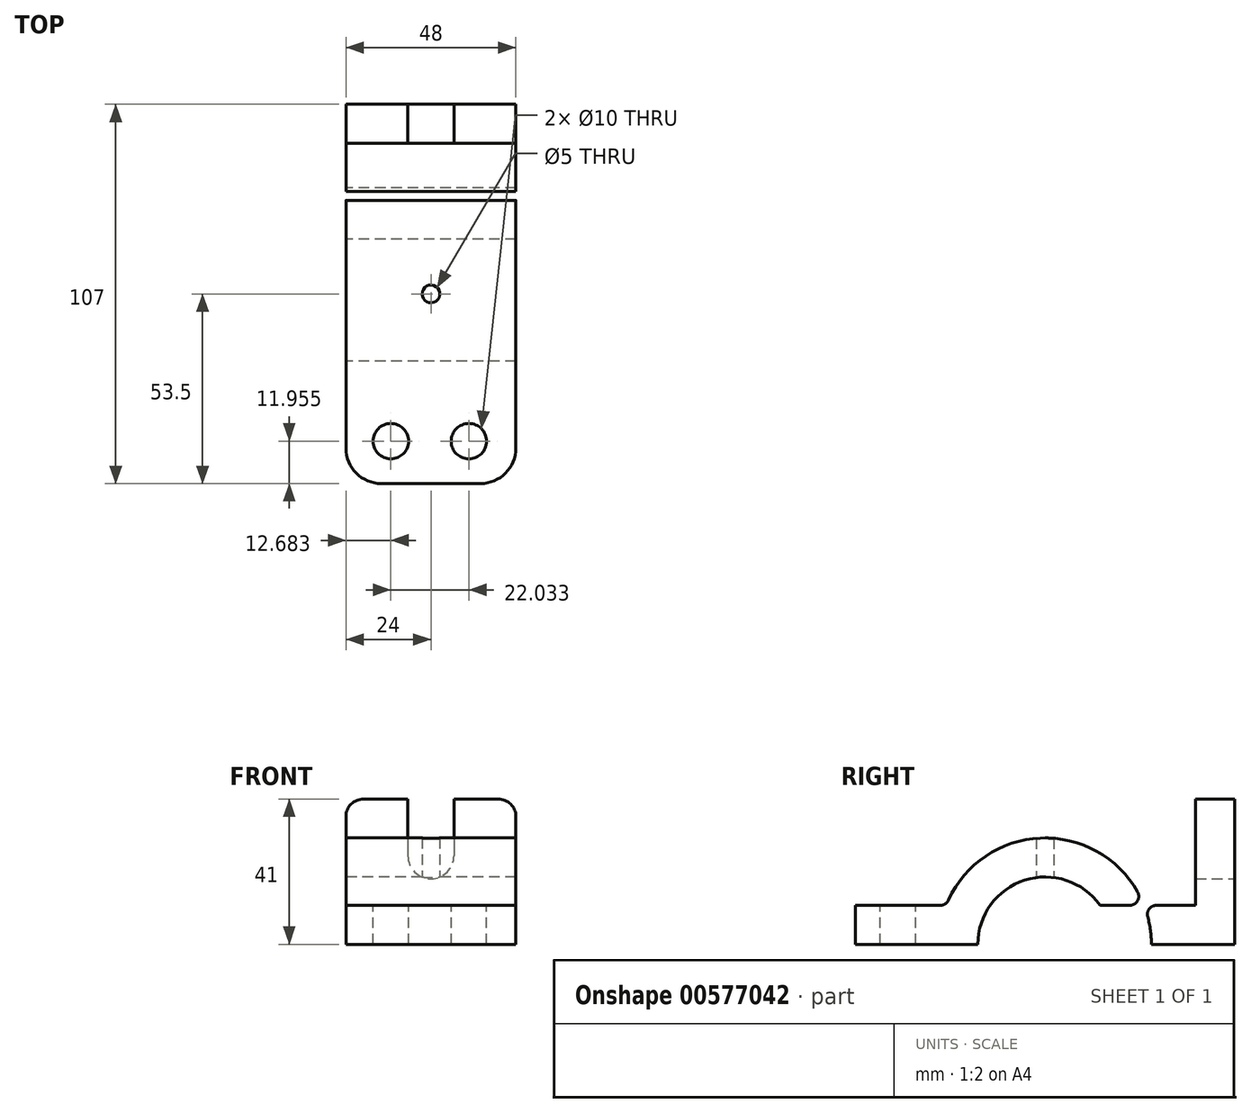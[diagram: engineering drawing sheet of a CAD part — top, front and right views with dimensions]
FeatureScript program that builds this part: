
annotation { "Feature Type Name" : "Feature", "Feature Type Description" : "" }
export const myFeature = defineFeature(function(context is Context, id is Id, definition is map)
    precondition{}
    {
        {
            var Q0;
            Q0=qCreatedBy(makeId("Right.planeOp"),FACE);
            var sketch = newSketch(context, id + "F0", { "sketchPlane" : qUnion([Q0])});
            skLineSegment(sketch, "E0", {"start": v(53.5, 0) * mm, "end": v(-53.5, 0) * mm});
            skLineSegment(sketch, "E1", {"start": v(0, 0) * mm, "end": v(53.5, 0) * mm});
            skArc(sketch, "E2", {"start": v(30, 0) * mm, "mid": v(0, 30) * mm, "end": v(-30, 0) * mm});
            skArc(sketch, "E3", {"start": v(19, 0) * mm, "mid": v(0, 19) * mm, "end": v(-19, 0) * mm});
            skLineSegment(sketch, "E4", {"start": v(53.5, 0) * mm, "end": v(53.5, 41) * mm});
            skLineSegment(sketch, "E5", {"start": v(53.5, 41) * mm, "end": v(42.5, 41) * mm});
            skLineSegment(sketch, "E6", {"start": v(42.5, 41) * mm, "end": v(42.5, 0) * mm});
            skLineSegment(sketch, "E7", {"start": v(-53.5, 0) * mm, "end": v(-53.5, 11) * mm});
            skLineSegment(sketch, "E8", {"start": v(-53.5, 11) * mm, "end": v(42.5, 11) * mm});
            skSolve(sketch);
        }
        {
            var Q0;
            {var subQ0=sQuery(id+"F0.wireOp",EDGE,"E7");Q0=makeQuery(id+"F0.imprint","IMPRINT",FACE,{"disambiguationData":[TD([[makeQuery(id+"F0.imprint","IMPRINT",EDGE,{"derivedFrom":subQ0}),-1.0]])]});}
            var Q1;
            {var subQ0=sQuery(id+"F0.wireOp",EDGE,"E2");var subQ1=sQuery(id+"F0.wireOp",EDGE,"E0");var subQ2=makeQuery(id+"F0.imprint","INTERSECT",VERTEX,{"derivedFrom":[subQ1,subQ0]});Q1=makeQuery(id+"F0.imprint","IMPRINT",FACE,{"disambiguationData":[TD([[makeQuery(id+"F0.imprint","IMPRINT",EDGE,{"disambiguationData":[TD([[subQ2,1.0]])],"derivedFrom":subQ1}),-1.0]])]});}
            var Q2;
            {var subQ0=sQuery(id+"F0.wireOp",EDGE,"E8");var subQ1=sQuery(id+"F0.wireOp",EDGE,"E2");var subQ2=makeQuery(id+"F0.imprint","INTERSECT",VERTEX,{"disambiguationData":[OD(0.0)],"derivedFrom":[subQ1,subQ0]});Q2=makeQuery(id+"F0.imprint","IMPRINT",FACE,{"disambiguationData":[TD([[makeQuery(id+"F0.imprint","IMPRINT",EDGE,{"disambiguationData":[TD([[subQ2,-1.0]])],"derivedFrom":subQ1}),1.0]])]});}
            var Q3;
            {var subQ0=sQuery(id+"F0.wireOp",EDGE,"E2");var subQ1=sQuery(id+"F0.wireOp",EDGE,"E1");var subQ2=makeQuery(id+"F0.imprint","INTERSECT",VERTEX,{"derivedFrom":[subQ1,subQ0]});Q3=makeQuery(id+"F0.imprint","IMPRINT",FACE,{"disambiguationData":[TD([[makeQuery(id+"F0.imprint","IMPRINT",EDGE,{"disambiguationData":[TD([[subQ2,1.0]])],"derivedFrom":subQ1}),1.0]])]});}
            var Q4;
            {var subQ0=sQuery(id+"F0.wireOp",EDGE,"E2");var subQ1=sQuery(id+"F0.wireOp",EDGE,"E1");var subQ2=makeQuery(id+"F0.imprint","INTERSECT",VERTEX,{"derivedFrom":[subQ1,subQ0]});Q4=makeQuery(id+"F0.imprint","IMPRINT",FACE,{"disambiguationData":[TD([[makeQuery(id+"F0.imprint","IMPRINT",EDGE,{"disambiguationData":[TD([[subQ2,-1.0]])],"derivedFrom":subQ1}),1.0]])]});}
            var Q5;
            {var subQ3=sQuery(id+"F0.wireOp",EDGE,"E4");Q5=makeQuery(id+"F0.imprint","IMPRINT",FACE,{"disambiguationData":[TD([[makeQuery(id+"F0.imprint","IMPRINT",EDGE,{"derivedFrom":subQ3}),1.0]])]});}
            extrude(context, id + "F1", {"entities" : qUnion([Q0, Q1, Q2, Q3, Q4, Q5]), "endBound" : BoundingType.SYMMETRIC, "depth" : 48 * mm, "offsetDistance" : 25.4 * mm});
        }
        {
            var Q0;
            Q0=makeQuery(id+"F1.opExtrude","CAP_EDGE",EDGE,{"disambiguationData":[OSD([sQuery(id+"F0.wireOp",EDGE,"E5")])],"isStart":false});
            fillet(context, id + "F2", {"entities" : qUnion([Q0]), "radius" : 5 * mm, "tangentPropagation" : true, "allowEdgeOverflow" : false});
        }
        {
            var Q0;
            Q0=makeQuery(id+"F1.opExtrude","CAP_EDGE",EDGE,{"disambiguationData":[OSD([sQuery(id+"F0.wireOp",EDGE,"E5")])],"isStart":true});
            fillet(context, id + "F3", {"entities" : qUnion([Q0]), "radius" : 5 * mm, "tangentPropagation" : true, "allowEdgeOverflow" : false});
        }
        {
            var Q0;
            Q0=makeQuery(id+"F1.opExtrude","SWEPT_FACE",FACE,{"disambiguationData":[OSD([sQuery(id+"F0.wireOp",EDGE,"E4")])]});
            var sketch = newSketch(context, id + "F4", { "sketchPlane" : qUnion([Q0])});
            skPoint(sketch, "E9", {"position": v(0, 41) * mm});
            skLineSegment(sketch, "E10", {"start": v(-6.5, 41) * mm, "end": v(6.5, 41) * mm});
            skLineSegment(sketch, "E11", {"start": v(0, 0) * mm, "end": v(0, 25) * mm});
            skLineSegment(sketch, "E12", {"start": v(-6.5, 41) * mm, "end": v(-6.5, 25) * mm});
            skLineSegment(sketch, "E13", {"start": v(6.5, 41) * mm, "end": v(6.5, 25) * mm});
            skCircle(sketch, "E14", {"center": v(0, 25) * mm, "radius": 6.5 * mm});
            skSolve(sketch);
        }
        {
            var Q0;
            {var subQ0=sQuery(id+"F4.wireOp",EDGE,"E14");var subQ1=makeQuery(id+"F4.imprint","INTERSECT",VERTEX,{"derivedFrom":[sQuery(id+"F4.wireOp",EDGE,"E12"),subQ0]});Q0=makeQuery(id+"F4.imprint","IMPRINT",FACE,{"disambiguationData":[TD([[makeQuery(id+"F4.imprint","IMPRINT",EDGE,{"disambiguationData":[TD([[subQ1,1.0]])],"derivedFrom":subQ0}),1.0]])]});}
            var Q1;
            Q1=makeQuery(id+"F4.imprint","IMPRINT",FACE,{"disambiguationData":[TD([[makeQuery(id+"F4.imprint","IMPRINT",EDGE,{"derivedFrom":sQuery(id+"F4.wireOp",EDGE,"E10")}),-1.0]])]});
            extrude(context, id + "F5", {"entities" : qUnion([Q0, Q1]), "operationType" : NewBodyOperationType.REMOVE, "oppositeDirection" : true, "depth" : 25.4 * mm, "offsetDistance" : 25.4 * mm});
        }
        {
            var Q0;
            {var subQ0=sQuery(id+"F0.wireOp",EDGE,"E8");Q0=makeQuery(id+"F1.opExtrude","SWEPT_FACE",FACE,{"disambiguationData":[OSD([subQ0]),TDD([makeQuery(id+"F0.imprint","IMPRINT",EDGE,{"disambiguationData":[TD([[makeQuery(id+"F0.imprint","INTERSECT",VERTEX,{"derivedFrom":[sQuery(id+"F0.wireOp",EDGE,"E7"),subQ0]}),-1.0]])],"derivedFrom":subQ0})])]});}
            var sketch = newSketch(context, id + "F6", { "sketchPlane" : qUnion([Q0])});
            skCircle(sketch, "E15", {"center": v(0, 0) * mm, "radius": 2.5 * mm});
            skSolve(sketch);
        }
        {
            var Q0;
            {var subQ0=sQuery(id+"F0.wireOp",EDGE,"E8");var subQ1=sQuery(id+"F0.wireOp",EDGE,"E2");Q0=makeQuery(id+"F1.opExtrude","SWEPT_EDGE",EDGE,{"disambiguationData":[OSD([subQ1,subQ0]),TDD([makeQuery(id+"F0.imprint","INTERSECT",VERTEX,{"disambiguationData":[OD(0.0)],"derivedFrom":[subQ1,subQ0]})])]});}
            var Q1;
            {var subQ0=sQuery(id+"F0.wireOp",EDGE,"E8");var subQ1=sQuery(id+"F0.wireOp",EDGE,"E2");Q1=makeQuery(id+"F1.opExtrude","SWEPT_EDGE",EDGE,{"disambiguationData":[OSD([subQ1,subQ0]),TDD([makeQuery(id+"F0.imprint","INTERSECT",VERTEX,{"disambiguationData":[OD(1.0)],"derivedFrom":[subQ1,subQ0]})])]});}
            fillet(context, id + "F7", {"entities" : qUnion([Q0, Q1]), "radius" : 2.54 * mm, "tangentPropagation" : true, "allowEdgeOverflow" : false});
        }
        {
            var Q0;
            Q0=makeQuery(id+"F6.imprint","IMPRINT",FACE,{"disambiguationData":[TD([[makeQuery(id+"F6.imprint","IMPRINT",EDGE,{"derivedFrom":sQuery(id+"F6.wireOp",EDGE,"E15")}),1.0]])]});
            extrude(context, id + "F8", {"entities" : qUnion([Q0]), "operationType" : NewBodyOperationType.REMOVE, "depth" : 25.4 * mm, "offsetDistance" : 25.4 * mm});
        }
        {
            var Q0;
            {var subQ0=sQuery(id+"F0.wireOp",EDGE,"E8");Q0=makeQuery(id+"F1.opExtrude","SWEPT_FACE",FACE,{"disambiguationData":[OSD([subQ0]),TDD([makeQuery(id+"F0.imprint","IMPRINT",EDGE,{"disambiguationData":[TD([[makeQuery(id+"F0.imprint","INTERSECT",VERTEX,{"derivedFrom":[sQuery(id+"F0.wireOp",EDGE,"E7"),subQ0]}),-1.0]])],"derivedFrom":subQ0})])]});}
            var sketch = newSketch(context, id + "F9", { "sketchPlane" : qUnion([Q0])});
            skCircle(sketch, "E16", {"center": v(-11.32, -41.54) * mm, "radius": 5 * mm});
            skCircle(sketch, "E17", {"center": v(10.72, -41.54) * mm, "radius": 5 * mm});
            skSolve(sketch);
        }
        {
            var Q0;
            Q0=makeQuery(id+"F1.opExtrude","CAP_EDGE",EDGE,{"disambiguationData":[OSD([sQuery(id+"F0.wireOp",EDGE,"E7")])],"isStart":true});
            var Q1;
            Q1=makeQuery(id+"F1.opExtrude","CAP_EDGE",EDGE,{"disambiguationData":[OSD([sQuery(id+"F0.wireOp",EDGE,"E7")])],"isStart":false});
            fillet(context, id + "F10", {"entities" : qUnion([Q0, Q1]), "radius" : 10 * mm, "tangentPropagation" : true, "allowEdgeOverflow" : false});
        }
        {
            var Q0;
            Q0=makeQuery(id+"F9.imprint","IMPRINT",FACE,{"disambiguationData":[TD([[makeQuery(id+"F9.imprint","IMPRINT",EDGE,{"derivedFrom":sQuery(id+"F9.wireOp",EDGE,"E16")}),1.0]])]});
            var Q1;
            Q1=makeQuery(id+"F9.imprint","IMPRINT",FACE,{"disambiguationData":[TD([[makeQuery(id+"F9.imprint","IMPRINT",EDGE,{"derivedFrom":sQuery(id+"F9.wireOp",EDGE,"E17")}),1.0]])]});
            extrude(context, id + "F11", {"entities" : qUnion([Q0, Q1]), "operationType" : NewBodyOperationType.REMOVE, "oppositeDirection" : true, "depth" : 25.4 * mm, "offsetDistance" : 25.4 * mm});
        }
    });
